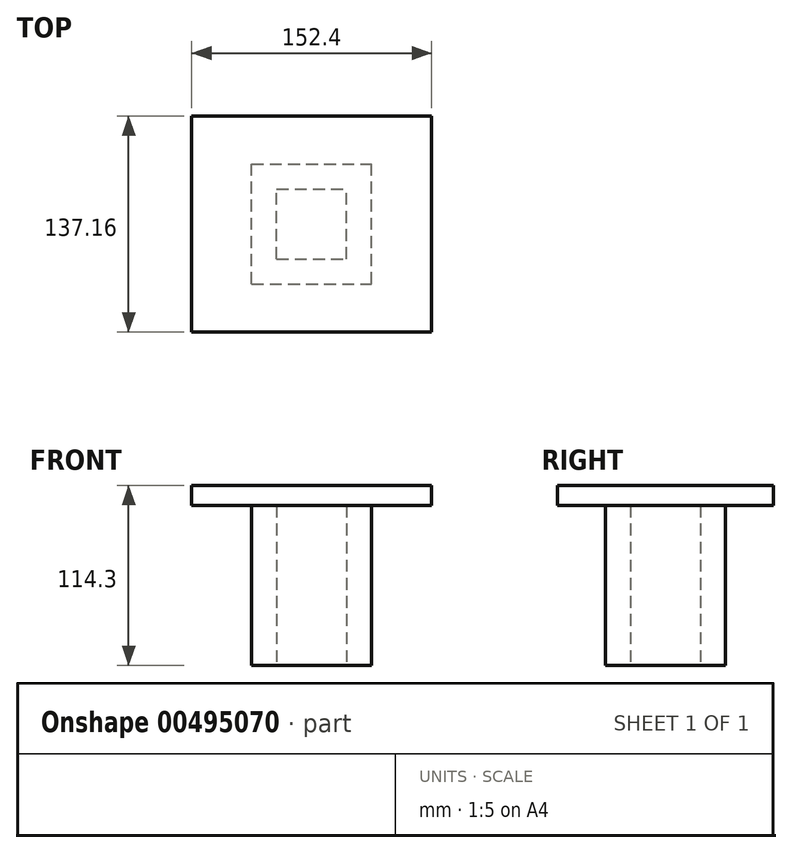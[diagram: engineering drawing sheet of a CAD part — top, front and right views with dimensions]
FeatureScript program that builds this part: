
annotation { "Feature Type Name" : "Feature", "Feature Type Description" : "" }
export const myFeature = defineFeature(function(context is Context, id is Id, definition is map)
    precondition{}
    {
        {
            var Q0;
            Q0=qCreatedBy(makeId("Front.planeOp"),FACE);
            var sketch = newSketch(context, id + "F0", { "sketchPlane" : qUnion([Q0])});
            skLineSegment(sketch, "E0.bottom", {"start": v(0, 0) * mm, "end": v(152.4, 0) * mm});
            skLineSegment(sketch, "E0.top", {"start": v(0, 12.7) * mm, "end": v(152.4, 12.7) * mm});
            skLineSegment(sketch, "E0.left", {"start": v(0, 0) * mm, "end": v(0, 12.7) * mm});
            skLineSegment(sketch, "E0.right", {"start": v(152.4, 0) * mm, "end": v(152.4, 12.7) * mm});
            skSolve(sketch);
        }
        {
            var Q0;
            Q0=makeQuery(id+"F0.imprint","IMPRINT",FACE,{"disambiguationData":[TD([[makeQuery(id+"F0.imprint","IMPRINT",EDGE,{"derivedFrom":sQuery(id+"F0.wireOp",EDGE,"E0.bottom")}),1.0]])]});
            extrude(context, id + "F1", {"entities" : qUnion([Q0]), "depth" : 137.16 * mm});
        }
        {
            var Q0;
            Q0=makeQuery(id+"F1.opExtrude","SWEPT_FACE",FACE,{"disambiguationData":[OSD([sQuery(id+"F0.wireOp",EDGE,"E0.bottom")])]});
            var sketch = newSketch(context, id + "F2", { "sketchPlane" : qUnion([Q0])});
            skLineSegment(sketch, "E1.bottom", {"start": v(38.1, 106.68) * mm, "end": v(114.3, 106.68) * mm});
            skLineSegment(sketch, "E1.top", {"start": v(38.1, 30.48) * mm, "end": v(114.3, 30.48) * mm});
            skLineSegment(sketch, "E1.left", {"start": v(38.1, 106.68) * mm, "end": v(38.1, 30.48) * mm});
            skLineSegment(sketch, "E1.right", {"start": v(114.3, 106.68) * mm, "end": v(114.3, 30.48) * mm});
            skSolve(sketch);
        }
        {
            var Q0;
            Q0=makeQuery(id+"F2.imprint","IMPRINT",FACE,{"disambiguationData":[TD([[makeQuery(id+"F2.imprint","IMPRINT",EDGE,{"derivedFrom":sQuery(id+"F2.wireOp",EDGE,"E1.bottom")}),-1.0]])]});
            extrude(context, id + "F3", {"entities" : qUnion([Q0]), "operationType" : NewBodyOperationType.ADD, "depth" : 101.6 * mm});
        }
        {
            var Q0;
            Q0=makeQuery(id+"F3.opExtrude","CAP_FACE",FACE,{"disambiguationData":[OSD([sQuery(id+"F2.wireOp",EDGE,"E1.bottom"),sQuery(id+"F2.wireOp",EDGE,"E1.top"),sQuery(id+"F2.wireOp",EDGE,"E1.left"),sQuery(id+"F2.wireOp",EDGE,"E1.right")])],"isStart":false});
            var sketch = newSketch(context, id + "F4", { "sketchPlane" : qUnion([Q0])});
            skLineSegment(sketch, "E2.bottom", {"start": v(53.98, 90.8) * mm, "end": v(98.43, 90.8) * mm});
            skLineSegment(sketch, "E2.top", {"start": v(53.98, 46.35) * mm, "end": v(98.43, 46.35) * mm});
            skLineSegment(sketch, "E2.left", {"start": v(53.98, 90.8) * mm, "end": v(53.98, 46.35) * mm});
            skLineSegment(sketch, "E2.right", {"start": v(98.43, 90.8) * mm, "end": v(98.43, 46.35) * mm});
            skSolve(sketch);
        }
        {
            var Q0;
            Q0=makeQuery(id+"F4.imprint","IMPRINT",FACE,{"disambiguationData":[TD([[makeQuery(id+"F4.imprint","IMPRINT",EDGE,{"derivedFrom":sQuery(id+"F4.wireOp",EDGE,"E2.bottom")}),-1.0]])]});
            extrude(context, id + "F5", {"entities" : qUnion([Q0]), "operationType" : NewBodyOperationType.REMOVE, "oppositeDirection" : true, "depth" : 101.6 * mm});
        }
    });
